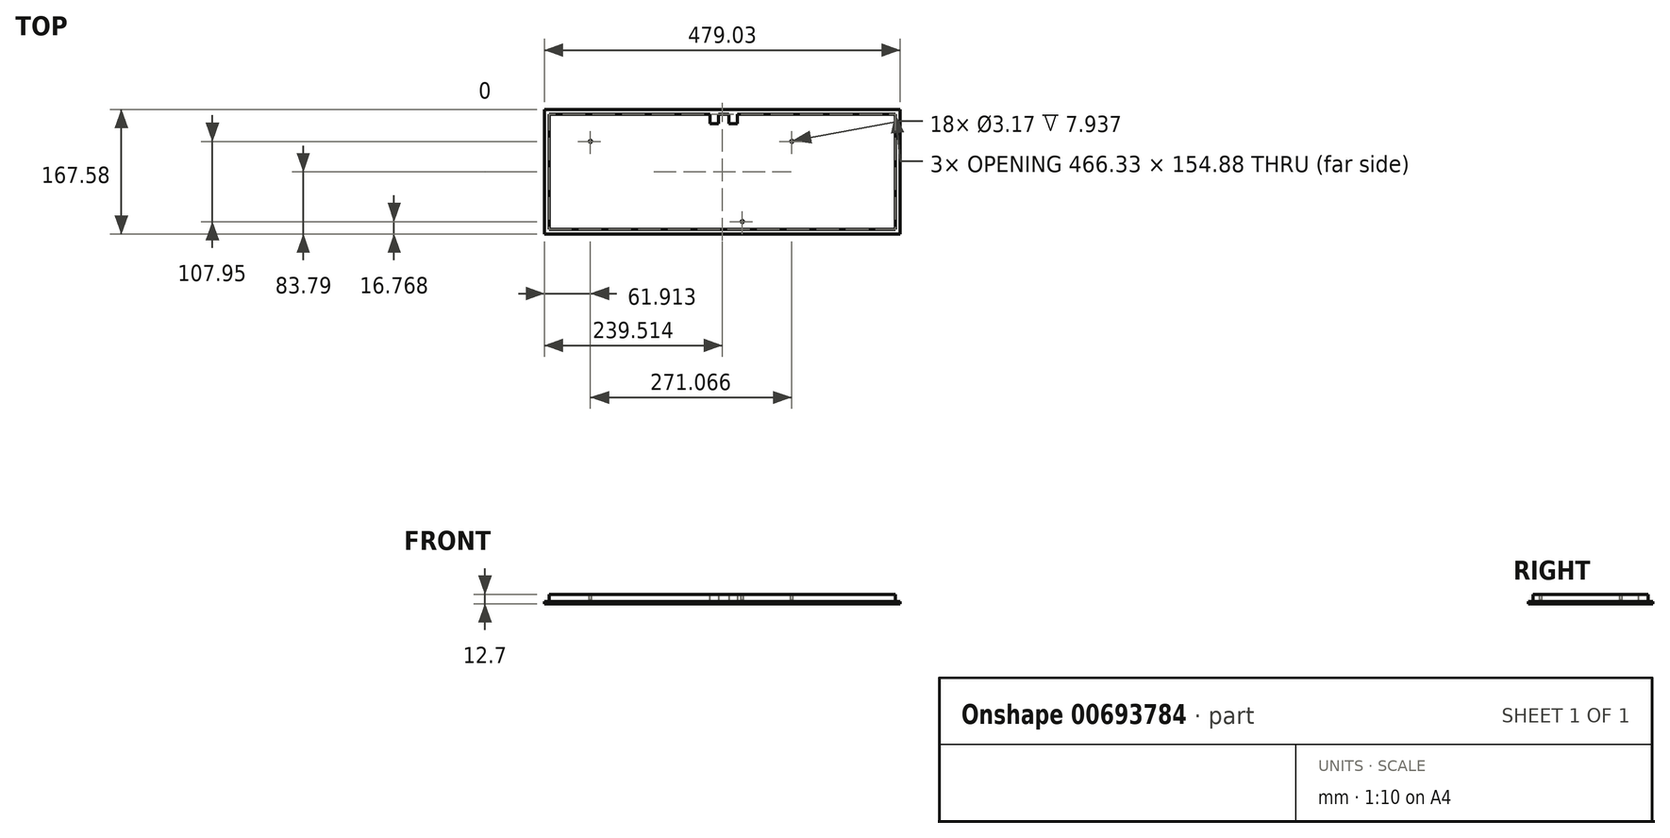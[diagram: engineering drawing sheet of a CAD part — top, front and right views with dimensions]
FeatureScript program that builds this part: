
annotation { "Feature Type Name" : "Feature", "Feature Type Description" : "" }
export const myFeature = defineFeature(function(context is Context, id is Id, definition is map)
    precondition{}
    {
        {
            var Q0;
            Q0=qCreatedBy(makeId("Top.planeOp"),FACE);
            var sketch = newSketch(context, id + "F0", { "sketchPlane" : qUnion([Q0])});
            skLineSegment(sketch, "E0.bottom", {"start": v(0, 0) * mm, "end": v(479.03, 0) * mm});
            skLineSegment(sketch, "E0.top", {"start": v(0, 167.58) * mm, "end": v(479.03, 167.58) * mm});
            skLineSegment(sketch, "E0.left", {"start": v(0, 0) * mm, "end": v(0, 167.58) * mm});
            skLineSegment(sketch, "E0.right", {"start": v(479.03, 0) * mm, "end": v(479.03, 167.58) * mm});
            skSolve(sketch);
        }
        {
            var Q0;
            Q0 = qSketchRegion(id + "F0", true);
            extrude(context, id + "F1", {"entities" : qUnion([Q0]), "depth" : 12.7 * mm, "offsetDistance" : 25.4 * mm});
        }
        {
            var Q0;
            Q0=makeQuery(id+"F1.opExtrude","CAP_FACE",FACE,{"disambiguationData":[OSD([sQuery(id+"F0.wireOp",EDGE,"E0.bottom"),sQuery(id+"F0.wireOp",EDGE,"E0.top"),sQuery(id+"F0.wireOp",EDGE,"E0.left"),sQuery(id+"F0.wireOp",EDGE,"E0.right")])],"isStart":false});
            var sketch = newSketch(context, id + "F2", { "sketchPlane" : qUnion([Q0])});
            skLineSegment(sketch, "E1.bottom", {"start": v(0, 0) * mm, "end": v(479.03, 0) * mm});
            skLineSegment(sketch, "E1.top", {"start": v(0, 167.58) * mm, "end": v(479.03, 167.58) * mm});
            skLineSegment(sketch, "E1.left", {"start": v(0, 0) * mm, "end": v(0, 167.58) * mm});
            skLineSegment(sketch, "E1.right", {"start": v(479.03, 0) * mm, "end": v(479.03, 167.58) * mm});
            skLineSegment(sketch, "E2.bottom", {"start": v(6.35, 6.35) * mm, "end": v(472.68, 6.35) * mm});
            skLineSegment(sketch, "E2.top", {"start": v(6.35, 161.23) * mm, "end": v(472.68, 161.23) * mm});
            skLineSegment(sketch, "E2.left", {"start": v(6.35, 6.35) * mm, "end": v(6.35, 161.23) * mm});
            skLineSegment(sketch, "E2.right", {"start": v(472.68, 6.35) * mm, "end": v(472.68, 161.23) * mm});
            skSolve(sketch);
        }
        {
            var Q0;
            Q0 = qSketchRegion(id + "F2", true);
            extrude(context, id + "F3", {"entities" : qUnion([Q0]), "operationType" : NewBodyOperationType.REMOVE, "oppositeDirection" : true, "depth" : 9.52 * mm, "offsetDistance" : 25.4 * mm});
        }
        {
            var Q0;
            Q0=makeQuery(id+"F1.opExtrude","SWEPT_FACE",FACE,{"disambiguationData":[OSD([sQuery(id+"F0.wireOp",EDGE,"E0.top")])]});
            var sketch = newSketch(context, id + "F4", { "sketchPlane" : qUnion([Q0])});
            skLineSegment(sketch, "E3.top", {"start": v(-234.16, 3.17) * mm, "end": v(-223.04, 3.18) * mm});
            skPoint(sketch, "E4", {"position": v(-228.6, 3.18) * mm});
            skLineSegment(sketch, "E5", {"start": v(-234.16, 3.18) * mm, "end": v(-234.16, 12.7) * mm});
            skLineSegment(sketch, "E6", {"start": v(-234.16, 12.7) * mm, "end": v(-223.04, 12.7) * mm});
            skLineSegment(sketch, "E7", {"start": v(-223.04, 12.7) * mm, "end": v(-223.04, 3.18) * mm});
            skLineSegment(sketch, "E8.bottom", {"start": v(-259.56, 3.18) * mm, "end": v(-248.44, 3.18) * mm});
            skLineSegment(sketch, "E8.top", {"start": v(-259.56, 12.7) * mm, "end": v(-248.44, 12.7) * mm});
            skLineSegment(sketch, "E8.left", {"start": v(-259.56, 3.18) * mm, "end": v(-259.56, 12.7) * mm});
            skLineSegment(sketch, "E8.right", {"start": v(-248.44, 3.18) * mm, "end": v(-248.44, 12.7) * mm});
            skSolve(sketch);
        }
        {
            var Q0;
            Q0 = qSketchRegion(id + "F4", true);
            extrude(context, id + "F5", {"entities" : qUnion([Q0]), "operationType" : NewBodyOperationType.REMOVE, "oppositeDirection" : true, "depth" : 19.05 * mm, "offsetDistance" : 25.4 * mm});
        }
        {
            var Q0;
            Q0=makeQuery(id+"F1.opExtrude","CAP_FACE",FACE,{"disambiguationData":[OSD([sQuery(id+"F0.wireOp",EDGE,"E0.bottom"),sQuery(id+"F0.wireOp",EDGE,"E0.top"),sQuery(id+"F0.wireOp",EDGE,"E0.left"),sQuery(id+"F0.wireOp",EDGE,"E0.right")])],"isStart":false});
            var sketch = newSketch(context, id + "F6", { "sketchPlane" : qUnion([Q0])});
            skCircle(sketch, "E9", {"center": v(61.91, 124.72) * mm, "radius": 1.59 * mm});
            skCircle(sketch, "E10", {"center": v(332.98, 124.72) * mm, "radius": 1.59 * mm});
            skCircle(sketch, "E11", {"center": v(266.3, 16.77) * mm, "radius": 1.59 * mm});
            skSolve(sketch);
        }
        {
            var Q0;
            Q0 = qSketchRegion(id + "F6", true);
            extrude(context, id + "F7", {"entities" : qUnion([Q0]), "operationType" : NewBodyOperationType.REMOVE, "oppositeDirection" : true, "depth" : 7.94 * mm, "offsetDistance" : 25.4 * mm});
        }
    });
